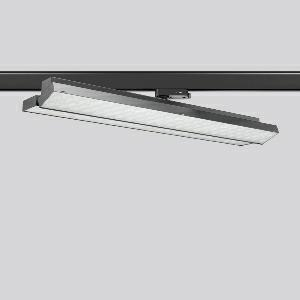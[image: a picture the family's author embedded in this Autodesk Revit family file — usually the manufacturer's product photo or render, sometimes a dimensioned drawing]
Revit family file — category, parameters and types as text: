
# Revit family: tx-move_742163_003_3_76_228d
name_source: partatom
category: Lighting Fixtures
units: mm (PartAtom-declared; Revit-internal decimal feet)

## family parameters
Cut with Voids When Loaded = No
Host = Face
Light Source = No
Part Type = Normal
Room Calculation Point = No
Round Connector Dimension = Use Diameter
Shared = No

## types (1)
- MultiLumen 1 (1 x LED Modul 835, 2875 lm, 3500)
    Apparent Load = 41 VA
    CIE Flux Codes = 65 90 98 100 100
    Color Rendering = 80
    Color Temperature = 3500
    Default Elevation = 1800 mm
    Description = Series: TX-MOVE
Multifunctional surface-mounted spotlight for area lighting. Very flat design. Housing: sheet steel, powder-coated. Rotation range: 356°. Swivel range: 90°. Consistent alignment possible with visible tilt scale. High-efficiency LED units with optimum light control thanks to clear plastic (PC) lens optics. Spezielle Mikrostrukturen reduzieren Gelbsaum. Asymmetrical light distribution. With adapter for RZB 3-circuit DALI tracks. Suitable for Track on ceiling. MultiLumen: Luminous flux adjustable in 3 steps. Factory setting is the highest luminous flux. Environmentally friendly and resource-saving due to replaceable and recyclable components. 
Colour: deep black, matt (RAL 9005)
Length: 570 mm
Width: 119 mm
Height: 88 mm
Lamp: LED
Socket: without socket
Colour temperature: 3500K
Colour rendering index (CRI): 80
System power: 41 W
Rated luminous flux: 5750 lm
Luminous efficiency: 140 lm/W
System power 2: 57 W
Rated luminous flux 2: 7750 lm
Luminous efficiency 2: 136 lm/W
System power 3: 73 W
Rated luminous flux 3: 9450 lm
Luminous efficiency 3: 129 lm/W
Control gear: Dimmable EVG, DALI
Protection class: I
Type of protection: IP 20
    Height = 75 mm
    Lamp = 1 x LED Modul 835
    Lamp Light Flux = 2875 lm
    Lamp count = 1
    Length = 569 mm
    Lifetime = 50000 h
    Luminous efficacy = 140 lm/W
    Manufacturer = RZB
    ModVariant = No
    Model = 742163.003.3.76
    Mounting Place = Ceiling
    Mounting Type = Rail mounted
    Number of Poles = 1
    OnlyDefault = Yes
    Power Factor = 1
    Product Name = TX-MOVE
    Product group = Track mounted projectors
    ProductGroupID = 301
    Protection Class = Protection class I
    Protection Degree = IP 20
    RLX_Detail_Level = 1
    RLX_Emergency_Light_Flux = 0 lm
    RLX_Emergency_Type = 0
    RLX_Emergency_Type_DB = No
    RlxData = <blob elided: 57405 chars, md5=473491f5>
    Socket = socket
    Standby Power = 0 W
    System Light Flux = 5750 lm
    System Power = 41 W
    Type Comments = MultiLumen 1
    Type Image = 742162.003.jpg
    URL = http://relux.com
    VarID = multilumen_1
    Voltage = 230 V
    Voltage Range = 220-240 V
    Weight = 0.00 kg
    Width = 119 mm

## geometry (parser evidence)
native form markers: Blend x4, Sweep x14
no freeform markers — native parametric forms only
